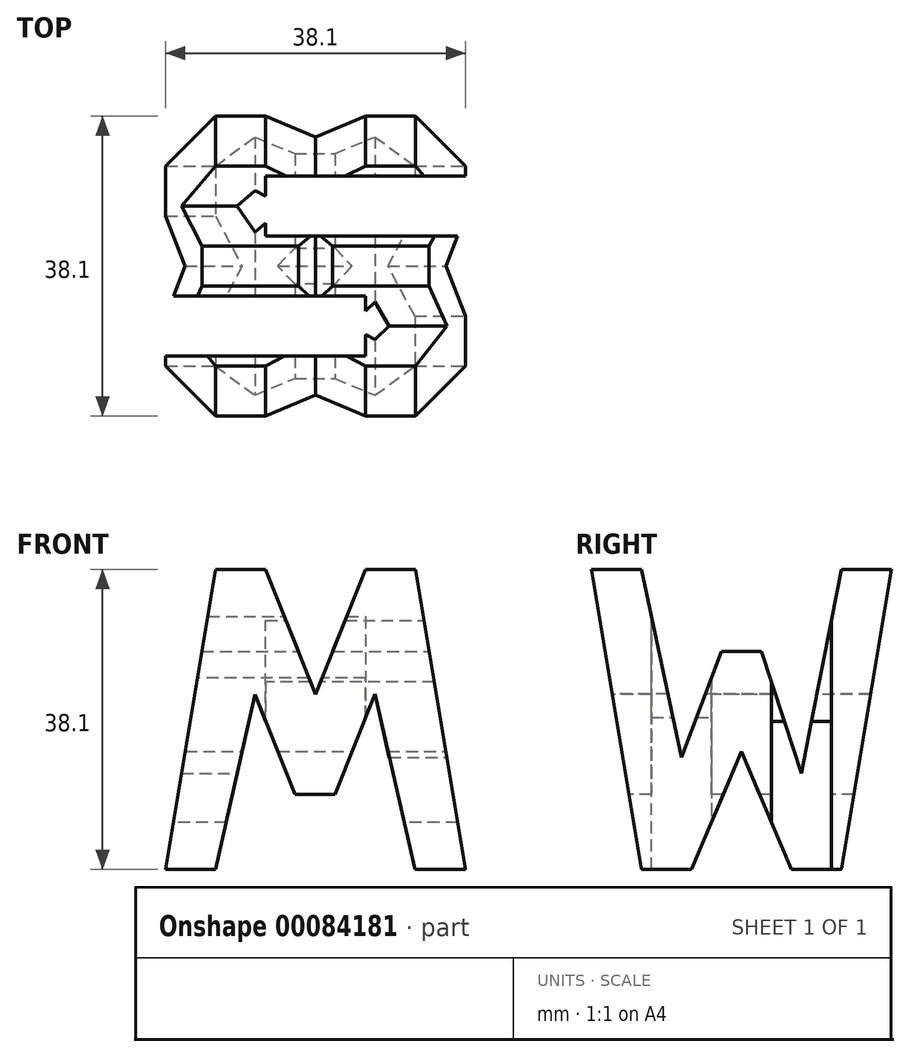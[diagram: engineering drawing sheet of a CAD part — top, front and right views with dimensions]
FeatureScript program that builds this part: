
annotation { "Feature Type Name" : "Feature", "Feature Type Description" : "" }
export const myFeature = defineFeature(function(context is Context, id is Id, definition is map)
    precondition{}
    {
        {
            var Q0;
            Q0=qCreatedBy(makeId("Front.planeOp"),FACE);
            var sketch = newSketch(context, id + "F0", { "sketchPlane" : qUnion([Q0])});
            skLineSegment(sketch, "E0", {"start": v(0, 0) * mm, "end": v(0, 38.1) * mm});
            skLineSegment(sketch, "E1", {"start": v(0, 38.1) * mm, "end": v(38.1, 38.1) * mm});
            skLineSegment(sketch, "E2", {"start": v(38.1, 38.1) * mm, "end": v(38.1, 0) * mm});
            skLineSegment(sketch, "E3", {"start": v(38.1, 0) * mm, "end": v(0, 0) * mm});
            skSolve(sketch);
        }
        {
            var Q0;
            Q0=makeQuery(id+"F0.imprint","IMPRINT",FACE,{"disambiguationData":[TD([[makeQuery(id+"F0.imprint","IMPRINT",EDGE,{"derivedFrom":sQuery(id+"F0.wireOp",EDGE,"E0")}),-1.0]])]});
            extrude(context, id + "F1", {"entities" : qUnion([Q0]), "depth" : 38.1 * mm});
        }
        {
            var Q0;
            Q0=qCreatedBy(makeId("Front.planeOp"),FACE);
            cPlane(context, id + "F2", {"entities" : qUnion([Q0]), "cplaneType" : CPlaneType.OFFSET, "offset" : 38.1 * mm, "width" : 152.4 * mm, "height" : 152.4 * mm});
        }
        {
            var Q0;
            Q0=qCreatedBy(makeId("Right.planeOp"),FACE);
            cPlane(context, id + "F3", {"entities" : qUnion([Q0]), "cplaneType" : CPlaneType.OFFSET, "offset" : 38.1 * mm, "width" : 152.4 * mm, "height" : 152.4 * mm});
        }
        {
            var Q0;
            Q0=qCreatedBy(makeId("Top.planeOp"),FACE);
            cPlane(context, id + "F4", {"entities" : qUnion([Q0]), "cplaneType" : CPlaneType.OFFSET, "offset" : 38.1 * mm, "width" : 152.4 * mm, "height" : 152.4 * mm});
        }
        {
            var Q0;
            Q0=qCreatedBy(id+"F3.planeOp",FACE);
            var sketch = newSketch(context, id + "F5", { "sketchPlane" : qUnion([Q0])});
            skLineSegment(sketch, "E4", {"start": v(0, 0) * mm, "end": v(0, 38.1) * mm});
            skLineSegment(sketch, "E5", {"start": v(0, 38.1) * mm, "end": v(-38.1, 38.1) * mm});
            skLineSegment(sketch, "E6", {"start": v(-38.1, 38.1) * mm, "end": v(-38.1, 0) * mm});
            skLineSegment(sketch, "E7", {"start": v(-38.1, 0) * mm, "end": v(0, 0) * mm});
            skLineSegment(sketch, "E8", {"start": v(-38.1, 38.1) * mm, "end": v(-31.75, 0) * mm});
            skLineSegment(sketch, "E9", {"start": v(-25.4, 0) * mm, "end": v(-19.05, 15) * mm});
            skLineSegment(sketch, "E10", {"start": v(-19.05, 15) * mm, "end": v(-19.05, 0) * mm});
            skLineSegment(sketch, "E11", {"start": v(-31.75, 38.1) * mm, "end": v(-26.67, 14.24) * mm});
            skLineSegment(sketch, "E12", {"start": v(-26.67, 14.24) * mm, "end": v(-21.59, 27.7) * mm});
            skLineSegment(sketch, "E13", {"start": v(-21.59, 27.7) * mm, "end": v(-16.5, 27.7) * mm});
            skLineSegment(sketch, "E14", {"start": v(-16.5, 27.7) * mm, "end": v(-11.43, 12.22) * mm});
            skLineSegment(sketch, "E15", {"start": v(-11.43, 12.22) * mm, "end": v(-6.35, 38.1) * mm});
            skLineSegment(sketch, "E16", {"start": v(-6.35, 38.1) * mm, "end": v(-11.43, 12.22) * mm});
            skLineSegment(sketch, "E17", {"start": v(-19.05, 15) * mm, "end": v(-12.7, 0) * mm});
            skLineSegment(sketch, "E18", {"start": v(0, 38.1) * mm, "end": v(-6.35, 0) * mm});
            skSolve(sketch);
        }
        {
            var Q0;
            {var subQ0=sQuery(id+"F5.wireOp",EDGE,"E11");Q0=makeQuery(id+"F5.imprint","IMPRINT",FACE,{"disambiguationData":[TD([[makeQuery(id+"F5.imprint","IMPRINT",EDGE,{"derivedFrom":subQ0}),1.0]])]});}
            var Q1;
            {var subQ0=sQuery(id+"F5.wireOp",EDGE,"E6");Q1=makeQuery(id+"F5.imprint","IMPRINT",FACE,{"disambiguationData":[TD([[makeQuery(id+"F5.imprint","IMPRINT",EDGE,{"derivedFrom":subQ0}),1.0]])]});}
            var Q2;
            {var subQ0=sQuery(id+"F5.wireOp",EDGE,"E9");Q2=makeQuery(id+"F5.imprint","IMPRINT",FACE,{"disambiguationData":[TD([[makeQuery(id+"F5.imprint","IMPRINT",EDGE,{"derivedFrom":subQ0}),-1.0]])]});}
            var Q3;
            {var subQ0=sQuery(id+"F5.wireOp",EDGE,"E10");Q3=makeQuery(id+"F5.imprint","IMPRINT",FACE,{"disambiguationData":[TD([[makeQuery(id+"F5.imprint","IMPRINT",EDGE,{"derivedFrom":subQ0}),1.0]])]});}
            var Q4;
            {var subQ0=sQuery(id+"F5.wireOp",EDGE,"E4");Q4=makeQuery(id+"F5.imprint","IMPRINT",FACE,{"disambiguationData":[TD([[makeQuery(id+"F5.imprint","IMPRINT",EDGE,{"derivedFrom":subQ0}),1.0]])]});}
            var Q5;
            Q5 = qSketchRegion(id + "F7", true);
            extrude(context, id + "F6", {"entities" : qUnion([Q0, Q1, Q2, Q3, Q4, Q5]), "operationType" : NewBodyOperationType.REMOVE, "oppositeDirection" : true, "depth" : 38.1 * mm});
        }
        {
            var Q0;
            Q0=qCreatedBy(id+"F2.planeOp",FACE);
            var sketch = newSketch(context, id + "F7", { "sketchPlane" : qUnion([Q0])});
            skLineSegment(sketch, "E19", {"start": v(0, 0) * mm, "end": v(0, 38.1) * mm});
            skLineSegment(sketch, "E20", {"start": v(0, 38.1) * mm, "end": v(38.1, 38.1) * mm});
            skLineSegment(sketch, "E21", {"start": v(38.1, 38.1) * mm, "end": v(38.1, 0) * mm});
            skLineSegment(sketch, "E22", {"start": v(38.1, 0) * mm, "end": v(0, 0) * mm});
            skLineSegment(sketch, "E23", {"start": v(0, 0) * mm, "end": v(6.35, 38.1) * mm});
            skLineSegment(sketch, "E24", {"start": v(6.35, 38.1) * mm, "end": v(12.7, 38.1) * mm});
            skLineSegment(sketch, "E25", {"start": v(25.4, 38.1) * mm, "end": v(31.75, 38.1) * mm});
            skLineSegment(sketch, "E26", {"start": v(31.75, 38.1) * mm, "end": v(38.1, 0) * mm});
            skLineSegment(sketch, "E27", {"start": v(26.58, 22.28) * mm, "end": v(31.66, 0) * mm});
            skPoint(sketch, "E28.end.orphan", {"position": v(19.05, 22.22) * mm});
            skLineSegment(sketch, "E29", {"start": v(16.42, 9.52) * mm, "end": v(21.5, 9.52) * mm});
            skLineSegment(sketch, "E30", {"start": v(21.5, 9.52) * mm, "end": v(26.58, 22.28) * mm});
            skLineSegment(sketch, "E31", {"start": v(12.7, 38.1) * mm, "end": v(19.05, 22.22) * mm});
            skPoint(sketch, "E31.endSnap0", {"position": v(19.05, 38.1) * mm});
            skPoint(sketch, "E32.start.orphan", {"position": v(6.35, 0) * mm});
            skLineSegment(sketch, "E33", {"start": v(6.35, 0) * mm, "end": v(11.34, 22.22) * mm});
            skLineSegment(sketch, "E34", {"start": v(11.34, 22.22) * mm, "end": v(16.42, 9.52) * mm});
            skLineSegment(sketch, "E35", {"start": v(25.4, 38.1) * mm, "end": v(19.05, 22.22) * mm});
            skSolve(sketch);
        }
        {
            var Q0;
            {var subQ0=sQuery(id+"F7.wireOp",EDGE,"E19");Q0=makeQuery(id+"F7.imprint","IMPRINT",FACE,{"disambiguationData":[TD([[makeQuery(id+"F7.imprint","IMPRINT",EDGE,{"derivedFrom":subQ0}),-1.0]])]});}
            var Q1;
            {var subQ0=sQuery(id+"F7.wireOp",EDGE,"E31");Q1=makeQuery(id+"F7.imprint","IMPRINT",FACE,{"disambiguationData":[TD([[makeQuery(id+"F7.imprint","IMPRINT",EDGE,{"derivedFrom":subQ0}),1.0]])]});}
            var Q2;
            {var subQ0=sQuery(id+"F7.wireOp",EDGE,"E21");Q2=makeQuery(id+"F7.imprint","IMPRINT",FACE,{"disambiguationData":[TD([[makeQuery(id+"F7.imprint","IMPRINT",EDGE,{"derivedFrom":subQ0}),-1.0]])]});}
            var Q3;
            {var subQ0=sQuery(id+"F7.wireOp",EDGE,"E27");Q3=makeQuery(id+"F7.imprint","IMPRINT",FACE,{"disambiguationData":[TD([[makeQuery(id+"F7.imprint","IMPRINT",EDGE,{"derivedFrom":subQ0}),-1.0]])]});}
            extrude(context, id + "F8", {"entities" : qUnion([Q0, Q1, Q2, Q3]), "operationType" : NewBodyOperationType.REMOVE, "oppositeDirection" : true, "depth" : 38.1 * mm});
        }
        {
            var Q0;
            Q0=qCreatedBy(id+"F4.planeOp",FACE);
            var sketch = newSketch(context, id + "F9", { "sketchPlane" : qUnion([Q0])});
            skLineSegment(sketch, "E36", {"start": v(0, 0) * mm, "end": v(38.1, 0) * mm});
            skLineSegment(sketch, "E37", {"start": v(38.1, 0) * mm, "end": v(38.1, -38.1) * mm});
            skLineSegment(sketch, "E38", {"start": v(38.1, -38.1) * mm, "end": v(0, -38.1) * mm});
            skLineSegment(sketch, "E39", {"start": v(0, -38.1) * mm, "end": v(0, 0) * mm});
            skLineSegment(sketch, "E40", {"start": v(38.1, -7.62) * mm, "end": v(12.7, -7.62) * mm});
            skLineSegment(sketch, "E41", {"start": v(12.7, -7.62) * mm, "end": v(12.7, -15.24) * mm});
            skLineSegment(sketch, "E42", {"start": v(12.7, -15.24) * mm, "end": v(38.1, -15.24) * mm});
            skLineSegment(sketch, "E43", {"start": v(0, -22.86) * mm, "end": v(25.4, -22.86) * mm});
            skLineSegment(sketch, "E44", {"start": v(25.4, -22.86) * mm, "end": v(25.4, -30.48) * mm});
            skLineSegment(sketch, "E45", {"start": v(25.4, -30.48) * mm, "end": v(0, -30.48) * mm});
            skSolve(sketch);
        }
        {
            var Q0;
            {var subQ0=sQuery(id+"F9.wireOp",EDGE,"E40");Q0=makeQuery(id+"F9.imprint","IMPRINT",FACE,{"disambiguationData":[TD([[makeQuery(id+"F9.imprint","IMPRINT",EDGE,{"derivedFrom":subQ0}),1.0]])]});}
            var Q1;
            {var subQ0=sQuery(id+"F9.wireOp",EDGE,"E43");Q1=makeQuery(id+"F9.imprint","IMPRINT",FACE,{"disambiguationData":[TD([[makeQuery(id+"F9.imprint","IMPRINT",EDGE,{"derivedFrom":subQ0}),-1.0]])]});}
            extrude(context, id + "F10", {"entities" : qUnion([Q0, Q1]), "operationType" : NewBodyOperationType.REMOVE, "oppositeDirection" : true, "depth" : 38.1 * mm});
        }
    });
